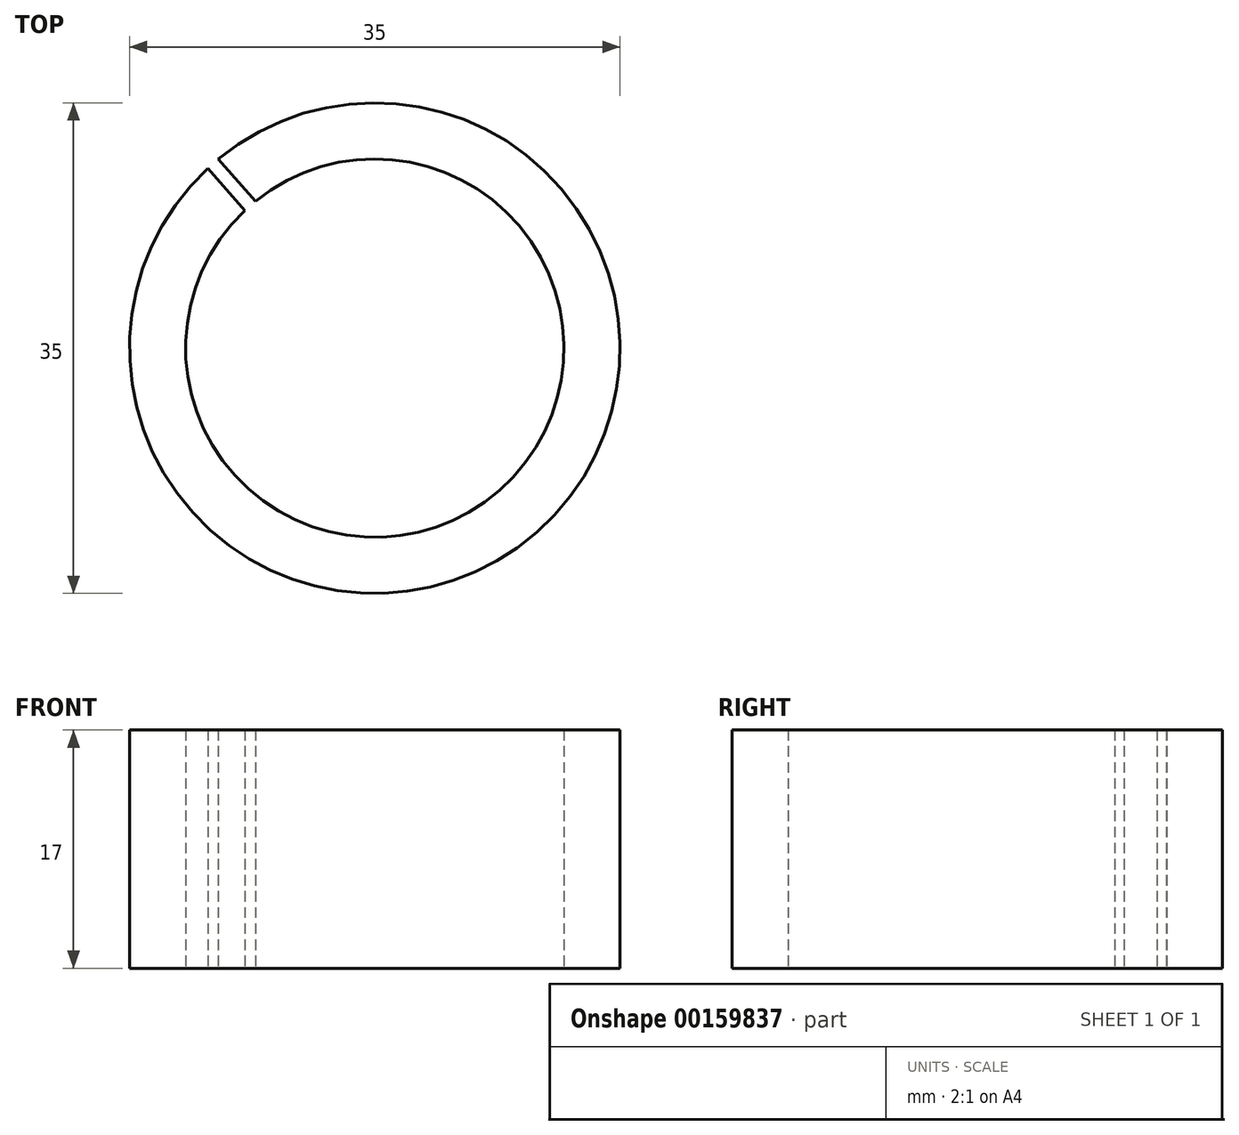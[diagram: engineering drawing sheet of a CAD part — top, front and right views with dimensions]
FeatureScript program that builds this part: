
annotation { "Feature Type Name" : "Feature", "Feature Type Description" : "" }
export const myFeature = defineFeature(function(context is Context, id is Id, definition is map)
    precondition{}
    {
        {
            var Q0;
            Q0=qCreatedBy(makeId("Top.planeOp"),FACE);
            var sketch = newSketch(context, id + "F0", { "sketchPlane" : qUnion([Q0])});
            skArc(sketch, "E0", {"start": v(-9.27, 9.81) * mm, "mid": v(8.9, -10.15) * mm, "end": v(-8.52, 10.47) * mm});
            skArc(sketch, "E1.0", {"start": v(-11.91, 12.82) * mm, "mid": v(11.54, -13.15) * mm, "end": v(-11.16, 13.48) * mm});
            skLineSegment(sketch, "E2", {"start": v(-8.52, 10.47) * mm, "end": v(-11.16, 13.48) * mm});
            skLineSegment(sketch, "E3", {"start": v(-9.27, 9.81) * mm, "end": v(-11.91, 12.82) * mm});
            skSolve(sketch);
        }
        {
            var Q0;
            Q0=makeQuery(id+"F0.imprint","IMPRINT",FACE,{"disambiguationData":[TD([[makeQuery(id+"F0.imprint","IMPRINT",EDGE,{"derivedFrom":sQuery(id+"F0.wireOp",EDGE,"E0")}),-1.0]])]});
            extrude(context, id + "F1", {"entities" : qUnion([Q0]), "depth" : 17 * mm});
        }
    });
